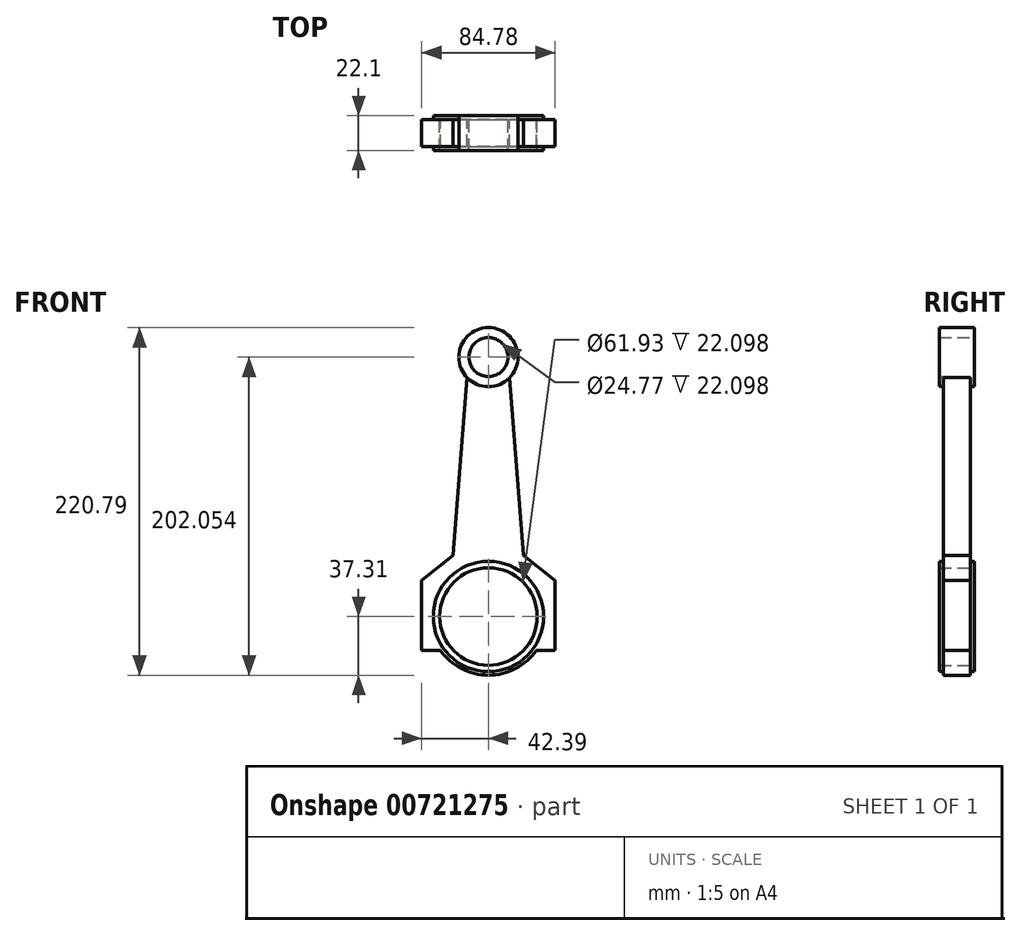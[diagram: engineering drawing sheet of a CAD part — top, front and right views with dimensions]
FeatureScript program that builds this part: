
annotation { "Feature Type Name" : "Feature", "Feature Type Description" : "" }
export const myFeature = defineFeature(function(context is Context, id is Id, definition is map)
    precondition{}
    {
        {
            var Q0;
            Q0=qCreatedBy(makeId("Front.planeOp"),FACE);
            var sketch = newSketch(context, id + "F0", { "sketchPlane" : qUnion([Q0])});
            skCircle(sketch, "E0", {"center": v(0, 164.74) * mm, "radius": 12.38 * mm});
            skCircle(sketch, "E1", {"center": v(0, 0) * mm, "radius": 30.96 * mm});
            skCircle(sketch, "E2.0", {"center": v(0, 164.74) * mm, "radius": 18.73 * mm});
            skArc(sketch, "E3.0", {"start": v(-30.44, -21.58) * mm, "mid": v(0, -37.31) * mm, "end": v(30.44, -21.58) * mm});
            skLineSegment(sketch, "E4", {"start": v(0, 0) * mm, "end": v(-42.4, 0) * mm});
            skLineSegment(sketch, "E5", {"start": v(-42.4, 0) * mm, "end": v(-42.4, 22.89) * mm});
            skLineSegment(sketch, "E6", {"start": v(-42.4, 22.89) * mm, "end": v(-22.35, 38.86) * mm});
            skLineSegment(sketch, "E7", {"start": v(-22.35, 38.86) * mm, "end": v(-13.45, 151.7) * mm});
            skLineSegment(sketch, "E8.MirrorCS", {"start": v(22.35, 38.86) * mm, "end": v(13.45, 151.7) * mm});
            skLineSegment(sketch, "E9.MirrorCS", {"start": v(42.4, 0) * mm, "end": v(42.4, 22.89) * mm});
            skLineSegment(sketch, "E10.MirrorCS", {"start": v(42.4, 22.89) * mm, "end": v(22.35, 38.86) * mm});
            skLineSegment(sketch, "E11.MirrorCS", {"start": v(0, 0) * mm, "end": v(42.4, 0) * mm});
            skLineSegment(sketch, "E12", {"start": v(-42.4, 0) * mm, "end": v(-42.4, -21.58) * mm});
            skLineSegment(sketch, "E13", {"start": v(-42.4, -21.58) * mm, "end": v(-30.44, -21.58) * mm});
            skLineSegment(sketch, "E14.MirrorCS", {"start": v(42.4, -21.58) * mm, "end": v(30.44, -21.58) * mm});
            skLineSegment(sketch, "E15.MirrorCS", {"start": v(42.4, 0) * mm, "end": v(42.4, -21.58) * mm});
            skCircle(sketch, "E16", {"center": v(0, 0) * mm, "radius": 35.03 * mm});
            skPoint(sketch, "E17.orphan", {"position": v(-12.34, 165.72) * mm});
            skPoint(sketch, "E18.orphan", {"position": v(12.34, 165.72) * mm});
            skSolve(sketch);
        }
        {
            var Q0;
            {var subQ0=sQuery(id+"F0.wireOp",EDGE,"E4");var subQ1=sQuery(id+"F0.wireOp",EDGE,"E1");var subQ2=makeQuery(id+"F0.imprint","INTERSECT",VERTEX,{"derivedFrom":[subQ1,subQ0]});Q0=makeQuery(id+"F0.imprint","IMPRINT",FACE,{"disambiguationData":[TD([[makeQuery(id+"F0.imprint","IMPRINT",EDGE,{"disambiguationData":[TD([[subQ2,1.0]])],"derivedFrom":subQ1}),-1.0]])]});}
            extrude(context, id + "F1", {"entities" : qUnion([Q0]), "endBound" : BoundingType.SYMMETRIC, "depth" : 22.1 * mm, "offsetDistance" : 25.4 * mm});
        }
        {
            var Q0;
            {var subQ0=sQuery(id+"F0.wireOp",EDGE,"E4");var subQ1=sQuery(id+"F0.wireOp",EDGE,"E1");var subQ2=makeQuery(id+"F0.imprint","INTERSECT",VERTEX,{"derivedFrom":[subQ1,subQ0]});Q0=makeQuery(id+"F0.imprint","IMPRINT",FACE,{"disambiguationData":[TD([[makeQuery(id+"F0.imprint","IMPRINT",EDGE,{"disambiguationData":[TD([[subQ2,-1.0]])],"derivedFrom":subQ1}),-1.0]])]});}
            extrude(context, id + "F2", {"entities" : qUnion([Q0]), "endBound" : BoundingType.SYMMETRIC, "depth" : 22.1 * mm, "offsetDistance" : 25.4 * mm});
        }
        {
            var Q0;
            {var subQ0=sQuery(id+"F0.wireOp",EDGE,"E5");Q0=makeQuery(id+"F0.imprint","IMPRINT",FACE,{"disambiguationData":[TD([[makeQuery(id+"F0.imprint","IMPRINT",EDGE,{"derivedFrom":subQ0}),-1.0]])]});}
            extrude(context, id + "F3", {"entities" : qUnion([Q0]), "operationType" : NewBodyOperationType.ADD, "endBound" : BoundingType.SYMMETRIC, "depth" : 17.02 * mm, "offsetDistance" : 25.4 * mm});
        }
        {
            var Q0;
            Q0=makeQuery(id+"F0.imprint","IMPRINT",FACE,{"disambiguationData":[TD([[makeQuery(id+"F0.imprint","IMPRINT",EDGE,{"derivedFrom":sQuery(id+"F0.wireOp",EDGE,"E0")}),-1.0]])]});
            extrude(context, id + "F4", {"entities" : qUnion([Q0]), "operationType" : NewBodyOperationType.ADD, "endBound" : BoundingType.SYMMETRIC, "depth" : 22.1 * mm, "offsetDistance" : 25.4 * mm});
        }
        {
            var Q0;
            Q0=makeQuery(id+"F0.imprint","IMPRINT",FACE,{"disambiguationData":[TD([[makeQuery(id+"F0.imprint","IMPRINT",EDGE,{"derivedFrom":sQuery(id+"F0.wireOp",EDGE,"E3.0")}),1.0]])]});
            extrude(context, id + "F5", {"entities" : qUnion([Q0]), "operationType" : NewBodyOperationType.ADD, "endBound" : BoundingType.SYMMETRIC, "depth" : 17.02 * mm, "offsetDistance" : 25.4 * mm});
        }
    });
